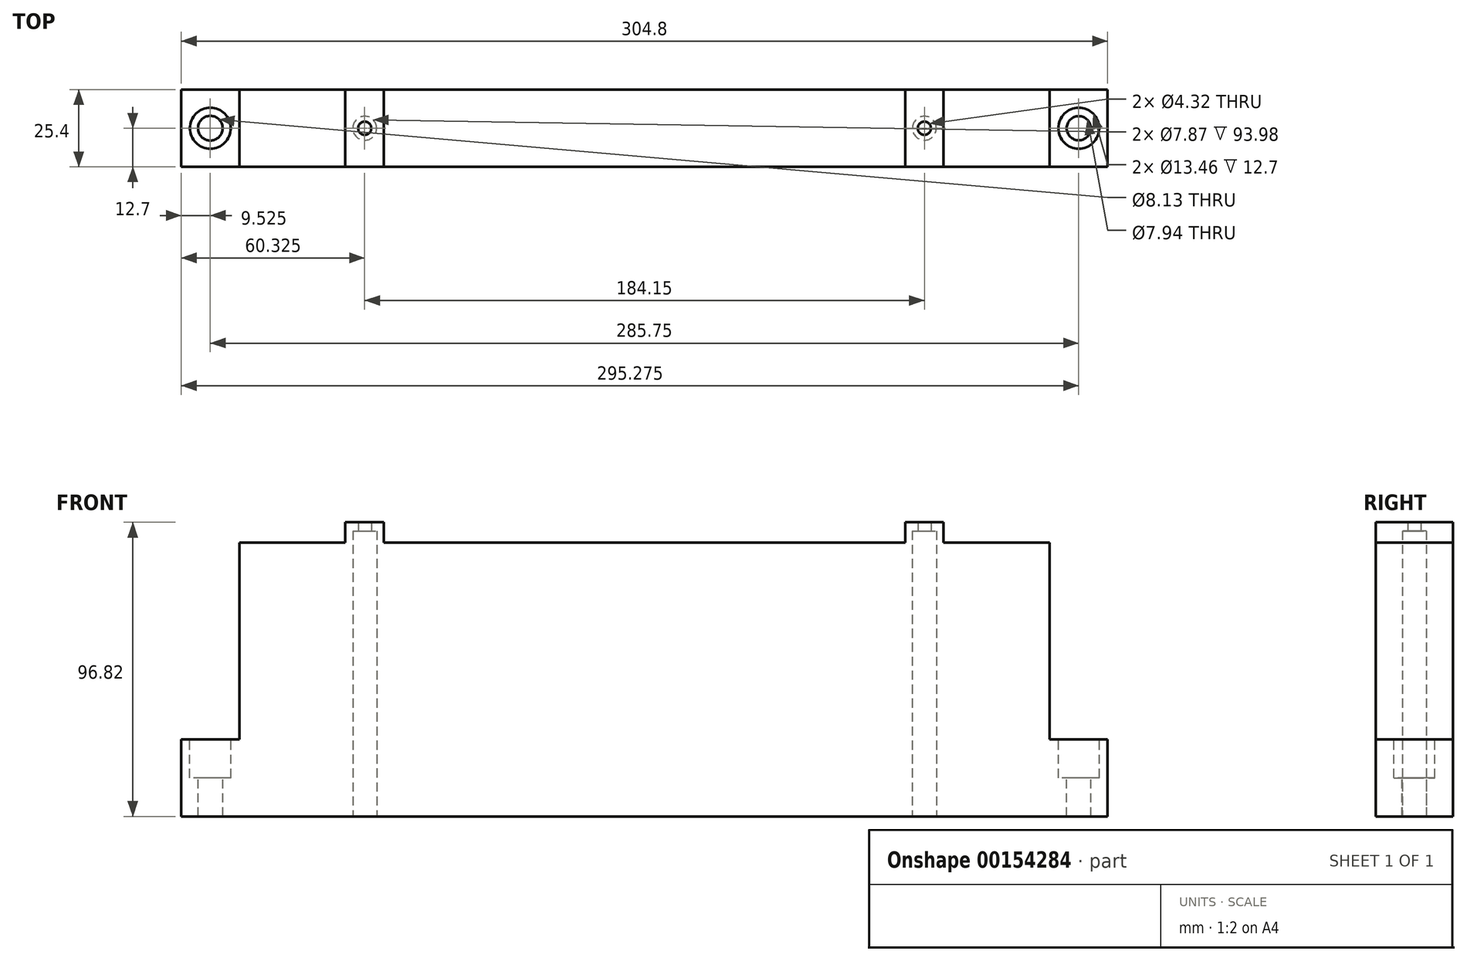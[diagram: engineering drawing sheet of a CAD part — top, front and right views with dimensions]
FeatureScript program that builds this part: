
annotation { "Feature Type Name" : "Feature", "Feature Type Description" : "" }
export const myFeature = defineFeature(function(context is Context, id is Id, definition is map)
    precondition{}
    {
        {
            var Q0;
            Q0=qCreatedBy(makeId("Top.planeOp"),FACE);
            var sketch = newSketch(context, id + "F0", { "sketchPlane" : qUnion([Q0])});
            skLineSegment(sketch, "E0.bottom", {"start": v(-152.4, 12.7) * mm, "end": v(152.4, 12.7) * mm});
            skLineSegment(sketch, "E0.top", {"start": v(-152.4, -12.7) * mm, "end": v(152.4, -12.7) * mm});
            skLineSegment(sketch, "E0.left", {"start": v(-152.4, 12.7) * mm, "end": v(-152.4, -12.7) * mm});
            skLineSegment(sketch, "E0.right", {"start": v(152.4, 12.7) * mm, "end": v(152.4, -12.7) * mm});
            skLineSegment(sketch, "E1", {"start": v(-152.4, 12.7) * mm, "end": v(152.4, -12.7) * mm, "construction": true});
            skSolve(sketch);
        }
        {
            var Q0;
            Q0=makeQuery(id+"F0.imprint","IMPRINT",FACE,{"disambiguationData":[TD([[makeQuery(id+"F0.imprint","IMPRINT",EDGE,{"derivedFrom":sQuery(id+"F0.wireOp",EDGE,"E0.bottom")}),-1.0]])]});
            extrude(context, id + "F1", {"entities" : qUnion([Q0]), "depth" : 96.82 * mm});
        }
        {
            var Q0;
            Q0=makeQuery(id+"F1.opExtrude","CAP_FACE",FACE,{"disambiguationData":[OSD([sQuery(id+"F0.wireOp",EDGE,"E0.bottom"),sQuery(id+"F0.wireOp",EDGE,"E0.top"),sQuery(id+"F0.wireOp",EDGE,"E0.left"),sQuery(id+"F0.wireOp",EDGE,"E0.right")])],"isStart":false});
            var sketch = newSketch(context, id + "F2", { "sketchPlane" : qUnion([Q0])});
            skLineSegment(sketch, "E2.bottom", {"start": v(-152.4, 12.7) * mm, "end": v(-133.35, 12.7) * mm});
            skLineSegment(sketch, "E2.top", {"start": v(-152.4, -12.7) * mm, "end": v(-133.35, -12.7) * mm});
            skLineSegment(sketch, "E2.left", {"start": v(-152.4, 12.7) * mm, "end": v(-152.4, -12.7) * mm});
            skLineSegment(sketch, "E2.right", {"start": v(-133.35, 12.7) * mm, "end": v(-133.35, -12.7) * mm});
            skLineSegment(sketch, "E3.bottom", {"start": v(152.4, 12.7) * mm, "end": v(133.35, 12.7) * mm});
            skLineSegment(sketch, "E3.top", {"start": v(152.4, -12.7) * mm, "end": v(133.35, -12.7) * mm});
            skLineSegment(sketch, "E3.left", {"start": v(152.4, 12.7) * mm, "end": v(152.4, -12.7) * mm});
            skLineSegment(sketch, "E3.right", {"start": v(133.35, 12.7) * mm, "end": v(133.35, -12.7) * mm});
            skSolve(sketch);
        }
        {
            var Q0;
            Q0=makeQuery(id+"F2.imprint","IMPRINT",FACE,{"disambiguationData":[TD([[makeQuery(id+"F2.imprint","IMPRINT",EDGE,{"derivedFrom":sQuery(id+"F2.wireOp",EDGE,"E2.bottom")}),-1.0]])]});
            var Q1;
            Q1=makeQuery(id+"F2.imprint","IMPRINT",FACE,{"disambiguationData":[TD([[makeQuery(id+"F2.imprint","IMPRINT",EDGE,{"derivedFrom":sQuery(id+"F2.wireOp",EDGE,"E3.bottom")}),-1.0]])]});
            extrude(context, id + "F3", {"entities" : qUnion([Q0, Q1]), "operationType" : NewBodyOperationType.REMOVE, "oppositeDirection" : true, "depth" : 71.42 * mm});
        }
        {
            var Q0;
            Q0=makeQuery(id+"F1.opExtrude","CAP_FACE",FACE,{"disambiguationData":[OSD([sQuery(id+"F0.wireOp",EDGE,"E0.bottom"),sQuery(id+"F0.wireOp",EDGE,"E0.top"),sQuery(id+"F0.wireOp",EDGE,"E0.left"),sQuery(id+"F0.wireOp",EDGE,"E0.right")])],"isStart":false});
            var sketch = newSketch(context, id + "F4", { "sketchPlane" : qUnion([Q0])});
            skLineSegment(sketch, "E4.bottom", {"start": v(-133.35, 12.7) * mm, "end": v(-98.43, 12.7) * mm});
            skLineSegment(sketch, "E4.top", {"start": v(-133.35, -12.7) * mm, "end": v(-98.43, -12.7) * mm});
            skLineSegment(sketch, "E4.left", {"start": v(-133.35, 12.7) * mm, "end": v(-133.35, -12.7) * mm});
            skLineSegment(sketch, "E4.right", {"start": v(-98.43, 12.7) * mm, "end": v(-98.43, -12.7) * mm});
            skLineSegment(sketch, "E5.bottom", {"start": v(133.35, 12.7) * mm, "end": v(98.43, 12.7) * mm});
            skLineSegment(sketch, "E5.top", {"start": v(133.35, -12.7) * mm, "end": v(98.43, -12.7) * mm});
            skLineSegment(sketch, "E5.left", {"start": v(133.35, 12.7) * mm, "end": v(133.35, -12.7) * mm});
            skLineSegment(sketch, "E5.right", {"start": v(98.43, 12.7) * mm, "end": v(98.43, -12.7) * mm});
            skLineSegment(sketch, "E6.bottom", {"start": v(-85.73, 12.7) * mm, "end": v(85.73, 12.7) * mm});
            skLineSegment(sketch, "E6.top", {"start": v(-85.73, -12.7) * mm, "end": v(85.73, -12.7) * mm});
            skLineSegment(sketch, "E6.left", {"start": v(-85.73, 12.7) * mm, "end": v(-85.73, -12.7) * mm});
            skLineSegment(sketch, "E6.right", {"start": v(85.73, 12.7) * mm, "end": v(85.73, -12.7) * mm});
            skSolve(sketch);
        }
        {
            var Q0;
            Q0=makeQuery(id+"F4.imprint","IMPRINT",FACE,{"disambiguationData":[TD([[makeQuery(id+"F4.imprint","IMPRINT",EDGE,{"derivedFrom":sQuery(id+"F4.wireOp",EDGE,"E4.bottom")}),-1.0]])]});
            var Q1;
            Q1=makeQuery(id+"F4.imprint","IMPRINT",FACE,{"disambiguationData":[TD([[makeQuery(id+"F4.imprint","IMPRINT",EDGE,{"derivedFrom":sQuery(id+"F4.wireOp",EDGE,"E6.bottom")}),-1.0]])]});
            var Q2;
            Q2=makeQuery(id+"F4.imprint","IMPRINT",FACE,{"disambiguationData":[TD([[makeQuery(id+"F4.imprint","IMPRINT",EDGE,{"derivedFrom":sQuery(id+"F4.wireOp",EDGE,"E5.bottom")}),-1.0]])]});
            extrude(context, id + "F5", {"entities" : qUnion([Q0, Q1, Q2]), "operationType" : NewBodyOperationType.REMOVE, "oppositeDirection" : true, "depth" : 6.65 * mm});
        }
        {
            var Q0;
            Q0=makeQuery(id+"F1.opExtrude","CAP_FACE",FACE,{"disambiguationData":[OSD([sQuery(id+"F0.wireOp",EDGE,"E0.bottom"),sQuery(id+"F0.wireOp",EDGE,"E0.top"),sQuery(id+"F0.wireOp",EDGE,"E0.left"),sQuery(id+"F0.wireOp",EDGE,"E0.right")])],"isStart":true});
            var sketch = newSketch(context, id + "F6", { "sketchPlane" : qUnion([Q0])});
            skLineSegment(sketch, "E7", {"start": v(-152.4, 0) * mm, "end": v(152.4, 0) * mm, "construction": true});
            skLineSegment(sketch, "E8", {"start": v(0, 12.7) * mm, "end": v(0, -12.7) * mm, "construction": true});
            skLineSegment(sketch, "E9", {"start": v(-142.88, 12.7) * mm, "end": v(-142.88, -12.7) * mm, "construction": true});
            skLineSegment(sketch, "E10", {"start": v(-92.08, 12.7) * mm, "end": v(-92.08, -12.7) * mm, "construction": true});
            skLineSegment(sketch, "E11", {"start": v(142.88, 12.7) * mm, "end": v(142.88, -12.7) * mm, "construction": true});
            skLineSegment(sketch, "E12", {"start": v(92.08, 12.7) * mm, "end": v(92.08, -12.7) * mm, "construction": true});
            skCircle(sketch, "E13", {"center": v(-92.08, 0) * mm, "radius": 2.16 * mm});
            skCircle(sketch, "E14", {"center": v(92.08, 0) * mm, "radius": 2.16 * mm});
            skSolve(sketch);
        }
        {
            var Q0;
            Q0=makeQuery(id+"F6.imprint","IMPRINT",FACE,{"disambiguationData":[TD([[makeQuery(id+"F6.imprint","IMPRINT",EDGE,{"derivedFrom":sQuery(id+"F6.wireOp",EDGE,"E13")}),1.0]])]});
            var Q1;
            Q1=makeQuery(id+"F6.imprint","IMPRINT",FACE,{"disambiguationData":[TD([[makeQuery(id+"F6.imprint","IMPRINT",EDGE,{"derivedFrom":sQuery(id+"F6.wireOp",EDGE,"E14")}),1.0]])]});
            extrude(context, id + "F7", {"entities" : qUnion([Q0, Q1]), "operationType" : NewBodyOperationType.REMOVE, "endBound" : BoundingType.THROUGH_ALL, "oppositeDirection" : true, "depth" : 25.4 * mm});
        }
        {
            var Q0;
            Q0=makeQuery(id+"F1.opExtrude","CAP_FACE",FACE,{"disambiguationData":[OSD([sQuery(id+"F0.wireOp",EDGE,"E0.bottom"),sQuery(id+"F0.wireOp",EDGE,"E0.top"),sQuery(id+"F0.wireOp",EDGE,"E0.left"),sQuery(id+"F0.wireOp",EDGE,"E0.right")])],"isStart":true});
            var sketch = newSketch(context, id + "F8", { "sketchPlane" : qUnion([Q0])});
            skCircle(sketch, "E15", {"center": v(-92.08, 0) * mm, "radius": 3.94 * mm});
            skCircle(sketch, "E16", {"center": v(92.08, 0) * mm, "radius": 3.94 * mm});
            skSolve(sketch);
        }
        {
            var Q0;
            Q0 = qSketchRegion(id + "F8", true);
            extrude(context, id + "F9", {"entities" : qUnion([Q0]), "operationType" : NewBodyOperationType.REMOVE, "oppositeDirection" : true, "depth" : 93.98 * mm});
        }
        {
            var Q0;
            Q0=makeQuery(id+"F3.boolean.opBoolean","COPY",FACE,{"derivedFrom":makeQuery(id+"F3.opExtrude","CAP_FACE",FACE,{"disambiguationData":[OSD([sQuery(id+"F2.wireOp",EDGE,"E2.bottom"),sQuery(id+"F2.wireOp",EDGE,"E2.top"),sQuery(id+"F2.wireOp",EDGE,"E2.left"),sQuery(id+"F2.wireOp",EDGE,"E2.right")])],"isStart":false})});
            var sketch = newSketch(context, id + "F10", { "sketchPlane" : qUnion([Q0])});
            skLineSegment(sketch, "E17", {"start": v(-152.4, 0) * mm, "end": v(152.67, 0) * mm, "construction": true});
            skPoint(sketch, "E18.centerSnap0", {"position": v(-142.87, 12.7) * mm});
            skLineSegment(sketch, "E19", {"start": v(142.88, 12.65) * mm, "end": v(142.88, -13.08) * mm, "construction": true});
            skLineSegment(sketch, "E20", {"start": v(0, 13.08) * mm, "end": v(0, -12.43) * mm, "construction": true});
            skLineSegment(sketch, "E21", {"start": v(-142.88, 12.7) * mm, "end": v(-142.88, -12.7) * mm, "construction": true});
            skCircle(sketch, "E22", {"center": v(-142.88, 0) * mm, "radius": 4.06 * mm});
            skCircle(sketch, "E23", {"center": v(-142.88, 0) * mm, "radius": 6.73 * mm});
            skCircle(sketch, "E24", {"center": v(142.88, 0) * mm, "radius": 3.97 * mm});
            skCircle(sketch, "E25", {"center": v(142.88, 0) * mm, "radius": 6.73 * mm});
            skSolve(sketch);
        }
        {
            var Q0;
            Q0=makeQuery(id+"F10.imprint","IMPRINT",FACE,{"disambiguationData":[TD([[makeQuery(id+"F10.imprint","IMPRINT",EDGE,{"derivedFrom":sQuery(id+"F10.wireOp",EDGE,"E24")}),1.0]])]});
            var Q1;
            Q1=makeQuery(id+"F10.imprint","IMPRINT",FACE,{"disambiguationData":[TD([[makeQuery(id+"F10.imprint","IMPRINT",EDGE,{"derivedFrom":sQuery(id+"F10.wireOp",EDGE,"E22")}),1.0]])]});
            extrude(context, id + "F11", {"entities" : qUnion([Q0, Q1]), "operationType" : NewBodyOperationType.REMOVE, "endBound" : BoundingType.THROUGH_ALL, "oppositeDirection" : true, "depth" : 25.4 * mm});
        }
        {
            var Q0;
            Q0 = qSketchRegion(id + "F10", true);
            extrude(context, id + "F12", {"entities" : qUnion([Q0]), "operationType" : NewBodyOperationType.REMOVE, "oppositeDirection" : true, "depth" : 12.7 * mm});
        }
    });
